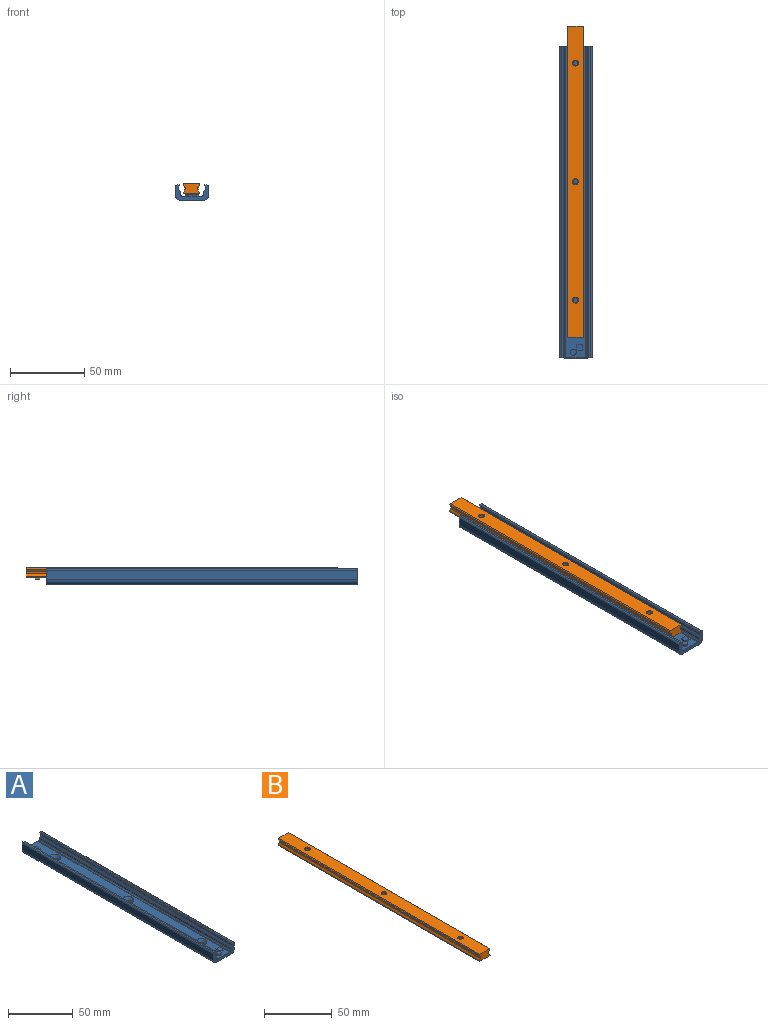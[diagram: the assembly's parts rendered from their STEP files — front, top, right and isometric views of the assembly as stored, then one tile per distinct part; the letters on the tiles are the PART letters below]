
ASSEMBLY  parts=2 mates=1
PART A: 46 faces, bbox 22x210x10.3 mm
  f0: cylinder r=0.43mm len=210mm, axis (0,1,0), area 197mm2, adj f34,f35,f44,f45
  f1: cylinder r=1.5mm len=210mm, axis (0,1,0), area 384.8mm2, adj f33,f34,f44,f45
  f2: cylinder r=1.5mm len=210mm, axis (0,1,0), area 384.8mm2, adj f22,f23,f44,f45
  f3: cylinder r=0.43mm len=210mm, axis (0,1,0), area 197mm2, adj f22,f43,f44,f45
  f4: cylinder r=2mm len=4mm, axis (0,0,-1), area 15.1mm2, adj f11,f29
  f5: cylinder r=2.4mm len=4.8mm, axis (0,0,-1), area 9.8mm2, adj f6,f39
  f6: cone r=3.47mm half-angle=45deg, axis (0,0,1), area 66.4mm2, adj f5,f29
  f7: cylinder r=2.4mm len=4.8mm, axis (0,0,-1), area 9.8mm2, adj f8,f39
  f8: cone r=3.47mm half-angle=45deg, axis (0,0,1), area 66.4mm2, adj f7,f29
  f9: cylinder r=2.4mm len=4.8mm, axis (0,0,-1), area 9.8mm2, adj f10,f39
  f10: cone r=3.47mm half-angle=45deg, axis (0,0,1), area 66.4mm2, adj f9,f29
  f11: plane 4x4mm, normal (0,0,1), area 12.6mm2, adj f4
  f12: plane 4x1.3mm, normal (1,0,0), area 5.2mm2, adj f13,f14,f15,f29
  f13: plane 4x1.3mm, normal (0,1,0), area 5.2mm2, adj f12,f15,f16,f29
  f14: plane 4x1.3mm, normal (0,-1,0), area 5.2mm2, adj f12,f15,f16,f29
  f15: plane 4x4mm, normal (0,0,1), area 16mm2, adj f12,f13,f14,f16
  f16: plane 4x1.3mm, normal (-1,0,0), area 5.2mm2, adj f13,f14,f15,f29
  f17: plane 4x1.3mm, normal (-1,0,0), area 5.2mm2, adj f18,f19,f20,f29
  f18: plane 4x1.3mm, normal (0,-1,0), area 5.2mm2, adj f17,f20,f21,f29
  f19: plane 4x1.3mm, normal (0,1,0), area 5.2mm2, adj f17,f20,f21,f29
  f20: plane 4x4mm, normal (0,0,1), area 16mm2, adj f17,f18,f19,f21
  f21: plane 4x1.3mm, normal (1,0,0), area 5.2mm2, adj f18,f19,f20,f29
  f22: plane 210x0.96mm, normal (-0.82,0,-0.57), area 246.9mm2, adj f2,f3,f44,f45
  f23: plane 210x1.38mm, normal (-0.82,0,0.57), area 352.9mm2, adj f2,f24,f44,f45
  f24: cylinder r=0.5mm len=210mm, axis (0,1,0), area 64.1mm2, adj f23,f25,f44,f45
  f25: plane 210x1.43mm, normal (-1,0,0), area 299.5mm2, adj f24,f26,f44,f45
  f26: cylinder r=1mm len=210mm, axis (0,1,0), area 329.9mm2, adj f25,f27,f44,f45
  f27: plane 210x0.3mm, normal (0,0,1), area 63mm2, adj f26,f28,f44,f45
  f28: cylinder r=0.2mm len=210mm, axis (0,1,0), area 131.9mm2, adj f27,f29,f44,f45
  f29: plane 210x13.3mm, normal (0,0,1), area 2553.4mm2, adj f4,f6,f8,f10,f12,f13,f14,f16
  f30: cylinder r=1mm len=210mm, axis (0,1,0), area 329.9mm2, adj f29,f31,f44,f45
  f31: plane 210x1.43mm, normal (1,0,0), area 299.5mm2, adj f30,f32,f44,f45
  f32: cylinder r=0.5mm len=210mm, axis (0,1,0), area 64.1mm2, adj f31,f33,f44,f45
  f33: plane 210x1.38mm, normal (0.82,0,0.57), area 352.9mm2, adj f1,f32,f44,f45
  f34: plane 210x0.96mm, normal (0.82,0,-0.57), area 246.9mm2, adj f0,f1,f44,f45
  f35: plane 210x1.27mm, normal (0,0,1), area 266.2mm2, adj f0,f36,f44,f45
  f36: cylinder r=1mm len=210mm, axis (0,1,0), area 329.9mm2, adj f35,f37,f44,f45
  f37: plane 210x6.25mm, normal (-1,0,0), area 1312.5mm2, adj f36,f38,f44,f45
  f38: cylinder r=3mm len=210mm, axis (0,1,0), area 989.6mm2, adj f37,f39,f44,f45
  f39: plane 210x16mm, normal (0,0,-1), area 3305.7mm2, adj f5,f7,f9,f38,f40,f44,f45
  f40: cylinder r=3mm len=210mm, axis (0,1,0), area 989.6mm2, adj f39,f41,f44,f45
  f41: plane 210x6.25mm, normal (1,0,0), area 1312.5mm2, adj f40,f42,f44,f45
  f42: cylinder r=1mm len=210mm, axis (0,1,0), area 329.9mm2, adj f41,f43,f44,f45
  f43: plane 210x1.27mm, normal (0,0,1), area 266.2mm2, adj f3,f42,f44,f45
  f44: plane 22x10.25mm, normal (0,1,0), area 94.6mm2, adj f0,f1,f2,f3,f22,f23,f24,f25
  f45: plane 22x10.25mm, normal (0,-1,0), area 94.6mm2, adj f0,f1,f2,f3,f22,f23,f24,f25
PART B: 33 faces, bbox 11.3x210x7.8 mm
  f0: cylinder r=1.5mm len=210mm, axis (0,1,0), area 384.8mm2, adj f29,f30,f31,f32
  f1: cylinder r=0.51mm len=210mm, axis (0,1,0), area 233.7mm2, adj f28,f29,f31,f32
  f2: cylinder r=0.51mm len=210mm, axis (0,1,0), area 233.7mm2, adj f27,f28,f31,f32
  f3: cylinder r=1.5mm len=210mm, axis (0,1,0), area 384.8mm2, adj f26,f27,f31,f32
  f4: cylinder r=0.5mm len=210mm, axis (0,1,0), area 229.1mm2, adj f25,f26,f31,f32
  f5: cylinder r=0.5mm len=210mm, axis (0,1,0), area 229.1mm2, adj f25,f30,f31,f32
  f6: cone r=1.81mm half-angle=45deg, axis (0,0,1), area 6.1mm2, adj f7,f28
  f7: cylinder r=1.62mm len=5.74mm, axis (0,0,1), area 58.5mm2, adj f6,f8
  f8: cone r=1.81mm half-angle=45deg, axis (0,0,-1), area 6.1mm2, adj f7,f25
  f9: cone r=1.81mm half-angle=45deg, axis (0,0,1), area 6.1mm2, adj f10,f28
  f10: cylinder r=1.62mm len=5.74mm, axis (0,0,1), area 58.5mm2, adj f9,f11
  f11: cone r=1.81mm half-angle=45deg, axis (0,0,-1), area 6.1mm2, adj f10,f25
  f12: cone r=1.81mm half-angle=45deg, axis (0,0,1), area 6.1mm2, adj f13,f28
  f13: cylinder r=1.62mm len=5.74mm, axis (0,0,1), area 58.5mm2, adj f12,f14
  f14: cone r=1.81mm half-angle=45deg, axis (0,0,-1), area 6.1mm2, adj f13,f25
  f15: plane 3x1.3mm, normal (-1,0,0), area 3.9mm2, adj f16,f17,f19,f25
  f16: plane 3x1.3mm, normal (0,1,0), area 3.9mm2, adj f15,f18,f19,f25
  f17: plane 3x1.3mm, normal (0,-1,0), area 3.9mm2, adj f15,f18,f19,f25
  f18: plane 3x1.3mm, normal (1,0,0), area 3.9mm2, adj f16,f17,f19,f25
  f19: plane 3x3mm, normal (0,0,-1), area 9mm2, adj f15,f16,f17,f18
  f20: plane 3x1.3mm, normal (1,0,0), area 3.9mm2, adj f21,f22,f24,f25
  f21: plane 3x1.3mm, normal (0,-1,0), area 3.9mm2, adj f20,f23,f24,f25
  f22: plane 3x1.3mm, normal (0,1,0), area 3.9mm2, adj f20,f23,f24,f25
  f23: plane 3x1.3mm, normal (-1,0,0), area 3.9mm2, adj f21,f22,f24,f25
  f24: plane 3x3mm, normal (0,0,-1), area 9mm2, adj f20,f21,f22,f23
  f25: plane 210x10.32mm, normal (0,0,-1), area 2111.2mm2, adj f4,f5,f8,f11,f14,f15,f16,f17
  f26: plane 210x1.6mm, normal (0.82,0,0.57), area 410.9mm2, adj f3,f4,f31,f32
  f27: plane 210x1.59mm, normal (0.82,0,-0.57), area 406.9mm2, adj f2,f3,f31,f32
  f28: plane 210x10.28mm, normal (0,0,1), area 2121.1mm2, adj f1,f2,f6,f9,f12,f31,f32
  f29: plane 210x1.59mm, normal (-0.82,0,-0.57), area 406.9mm2, adj f0,f1,f31,f32
  f30: plane 210x1.6mm, normal (-0.82,0,0.57), area 410.9mm2, adj f0,f5,f31,f32
  f31: plane 11.32x6.5mm, normal (0,1,0), area 64.3mm2, adj f0,f1,f2,f3,f4,f5,f25,f26
  f32: plane 11.32x6.5mm, normal (0,-1,0), area 64.3mm2, adj f0,f1,f2,f3,f4,f5,f25,f26
PLACE A at identity fixed
PLACE B t=(-0.35,-96.97,0)mm
MATE slider A.f45 <-> B.f32  axis (0,-1,0) through (-0.35,-111,-8.2)mm
